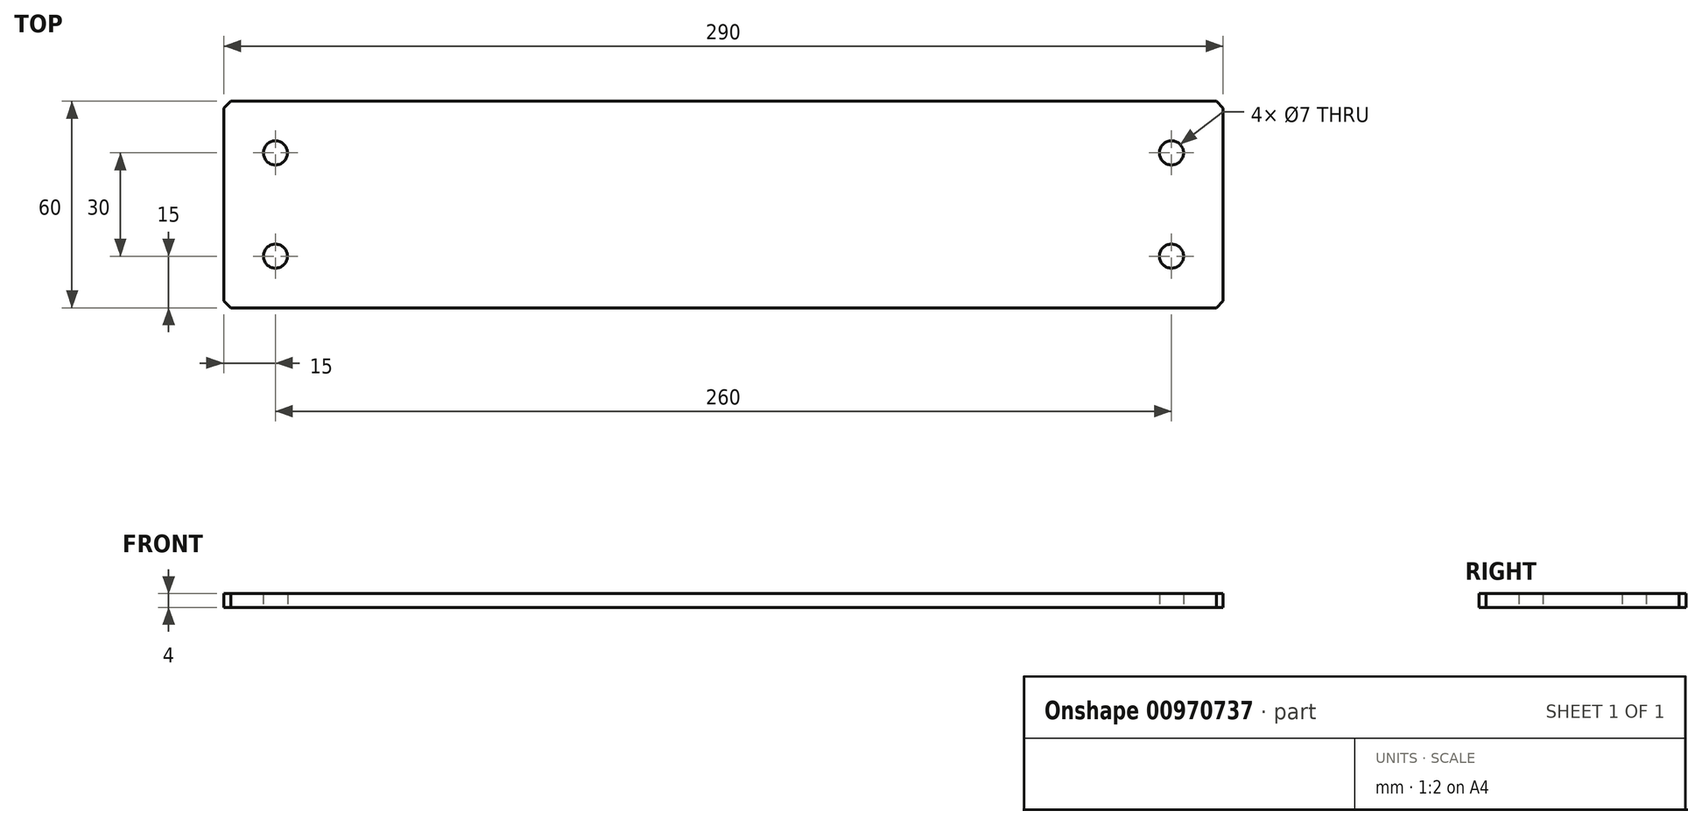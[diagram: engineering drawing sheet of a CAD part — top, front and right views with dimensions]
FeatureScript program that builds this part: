
annotation { "Feature Type Name" : "Feature", "Feature Type Description" : "" }
export const myFeature = defineFeature(function(context is Context, id is Id, definition is map)
    precondition{}
    {
        {
            var Q0;
            Q0=qCreatedBy(makeId("Top.planeOp"),FACE);
            var sketch = newSketch(context, id + "F0", { "sketchPlane" : qUnion([Q0])});
            skLineSegment(sketch, "E0.bottom", {"start": v(145, -30) * mm, "end": v(-145, -30) * mm});
            skLineSegment(sketch, "E0.top", {"start": v(145, 30) * mm, "end": v(-145, 30) * mm});
            skLineSegment(sketch, "E0.left", {"start": v(145, -30) * mm, "end": v(145, 30) * mm});
            skLineSegment(sketch, "E0.right", {"start": v(-145, -30) * mm, "end": v(-145, 30) * mm});
            skPoint(sketch, "E0.middle", {"position": v(0, 0) * mm});
            skLineSegment(sketch, "E1.bottom", {"start": v(130, -15) * mm, "end": v(-130, -15) * mm, "construction": true});
            skLineSegment(sketch, "E1.top", {"start": v(130, 15) * mm, "end": v(-130, 15) * mm, "construction": true});
            skLineSegment(sketch, "E1.left", {"start": v(130, -15) * mm, "end": v(130, 15) * mm, "construction": true});
            skLineSegment(sketch, "E1.right", {"start": v(-130, -15) * mm, "end": v(-130, 15) * mm, "construction": true});
            skCircle(sketch, "E2", {"center": v(-130, 15) * mm, "radius": 3.5 * mm});
            skCircle(sketch, "E3", {"center": v(-130, -15) * mm, "radius": 3.5 * mm});
            skCircle(sketch, "E4", {"center": v(130, 15) * mm, "radius": 3.5 * mm});
            skCircle(sketch, "E5", {"center": v(130, -15) * mm, "radius": 3.5 * mm});
            skSolve(sketch);
        }
        {
            var Q0;
            Q0=makeQuery(id+"F0.imprint","IMPRINT",FACE,{"disambiguationData":[TD([[makeQuery(id+"F0.imprint","IMPRINT",EDGE,{"derivedFrom":sQuery(id+"F0.wireOp",EDGE,"E0.bottom")}),-1.0]])]});
            extrude(context, id + "F1", {"entities" : qUnion([Q0]), "depth" : 4 * mm, "offsetDistance" : 25 * mm});
        }
        {
            var Q0;
            Q0=makeQuery(id+"F1.opExtrude","SWEPT_EDGE",EDGE,{"disambiguationData":[OSD([sQuery(id+"F0.wireOp",EDGE,"E0.top"),sQuery(id+"F0.wireOp",EDGE,"E0.right")])]});
            var Q1;
            Q1=makeQuery(id+"F1.opExtrude","SWEPT_EDGE",EDGE,{"disambiguationData":[OSD([sQuery(id+"F0.wireOp",EDGE,"E0.bottom"),sQuery(id+"F0.wireOp",EDGE,"E0.right")])]});
            var Q2;
            Q2=makeQuery(id+"F1.opExtrude","SWEPT_EDGE",EDGE,{"disambiguationData":[OSD([sQuery(id+"F0.wireOp",EDGE,"E0.top"),sQuery(id+"F0.wireOp",EDGE,"E0.left")])]});
            var Q3;
            Q3=makeQuery(id+"F1.opExtrude","SWEPT_EDGE",EDGE,{"disambiguationData":[OSD([sQuery(id+"F0.wireOp",EDGE,"E0.bottom"),sQuery(id+"F0.wireOp",EDGE,"E0.left")])]});
            chamfer(context, id + "F2", {"entities" : qUnion([Q0, Q1, Q2, Q3]), "width" : 2 * mm, "tangentPropagation" : true});
        }
    });
